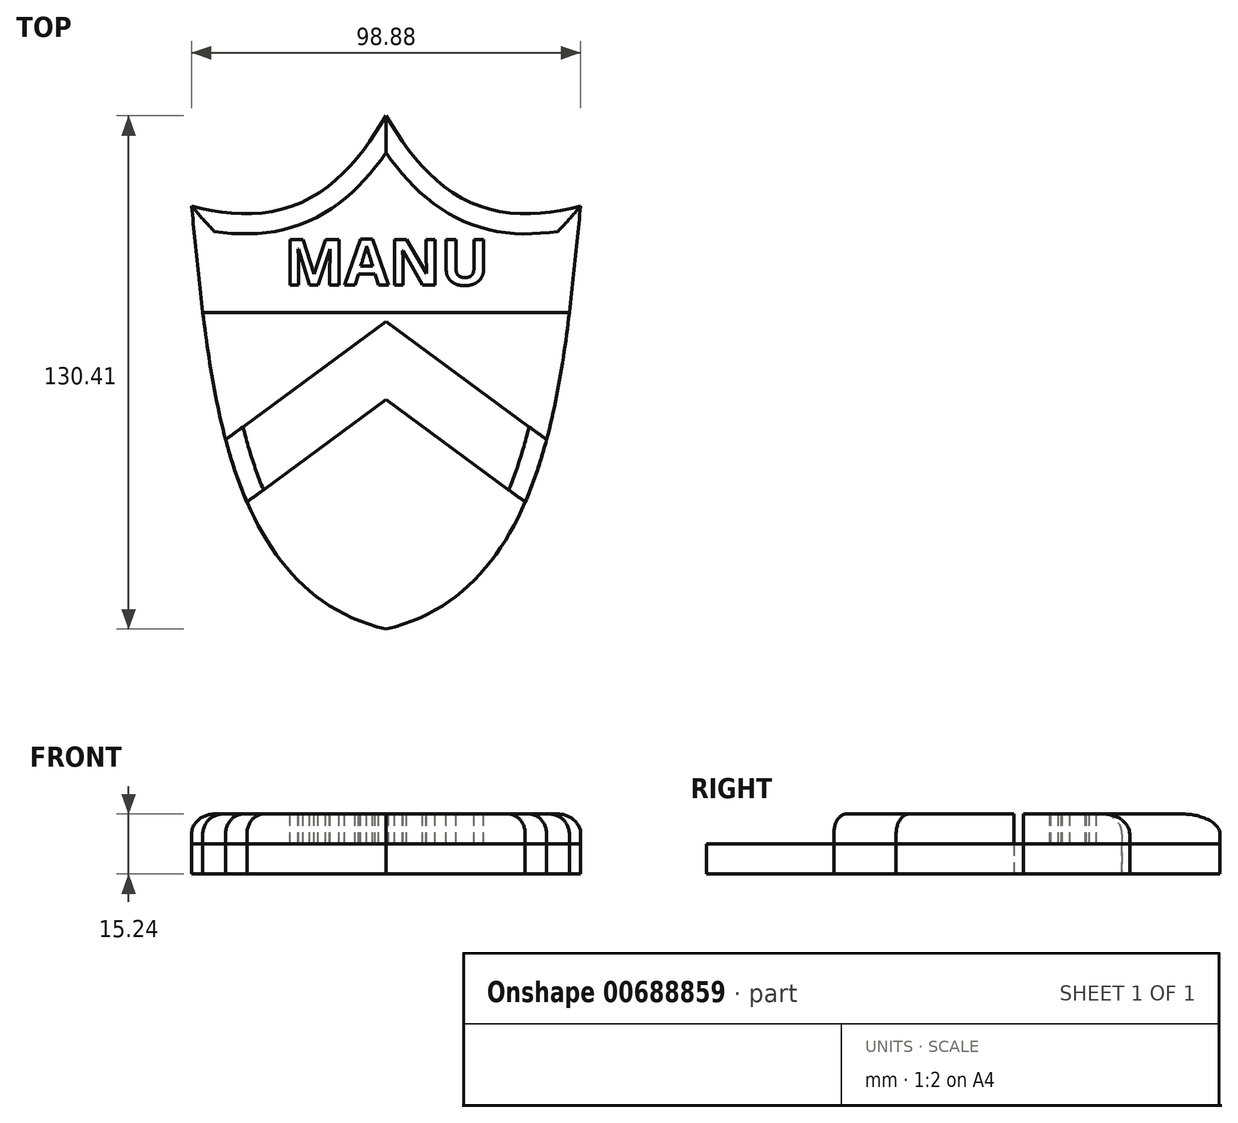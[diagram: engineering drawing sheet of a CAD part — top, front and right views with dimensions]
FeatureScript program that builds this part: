
annotation { "Feature Type Name" : "Feature", "Feature Type Description" : "" }
export const myFeature = defineFeature(function(context is Context, id is Id, definition is map)
    precondition{}
    {
        {
            var Q0;
            Q0=qCreatedBy(makeId("Top.planeOp"),FACE);
            var sketch = newSketch(context, id + "F0", { "sketchPlane" : qUnion([Q0])});
            skFitSpline(sketch, "E0", {"points": [v(-49.44, 33.32) * mm, v(0, -74.16) * mm], "startDerivative": vector(12.9, -119.66) * mm, "endDerivative": vector(128.25, -30.1) * mm});
            skFitSpline(sketch, "E1", {"points": [v(-49.44, 33.32) * mm, v(0, 56.25) * mm], "startDerivative": vector(78.1, -20.78) * mm, "endDerivative": vector(31.53, 53.02) * mm});
            skFitSpline(sketch, "E2.MirrorCS", {"points": [v(49.44, 33.32) * mm, v(0, 56.25) * mm], "startDerivative": vector(-78.1, -20.78) * mm, "endDerivative": vector(-31.53, 53.02) * mm});
            skFitSpline(sketch, "E3.MirrorCS", {"points": [v(49.44, 33.32) * mm, v(0, -74.16) * mm], "startDerivative": vector(-12.9, -119.66) * mm, "endDerivative": vector(-128.25, -30.1) * mm});
            skLineSegment(sketch, "E4", {"start": v(-46.57, 6.3) * mm, "end": v(0, 6.3) * mm});
            skLineSegment(sketch, "E5.MirrorCS", {"start": v(46.57, 6.3) * mm, "end": v(0, 6.3) * mm});
            skLineSegment(sketch, "E6", {"start": v(-40.76, -26.02) * mm, "end": v(0, 3.94) * mm});
            skLineSegment(sketch, "E7", {"start": v(-35.35, -41.87) * mm, "end": v(0, -15.88) * mm});
            skLineSegment(sketch, "E8.MirrorCS", {"start": v(40.76, -26.02) * mm, "end": v(0, 3.94) * mm});
            skLineSegment(sketch, "E9.MirrorCS", {"start": v(35.35, -41.87) * mm, "end": v(0, -15.88) * mm});
            skSolve(sketch);
        }
        {
            var Q0;
            {var subQ3=sQuery(id+"F0.wireOp",EDGE,"E1");Q0=makeQuery(id+"F0.imprint","IMPRINT",FACE,{"disambiguationData":[TD([[makeQuery(id+"F0.imprint","IMPRINT",EDGE,{"derivedFrom":subQ3}),-1.0]])]});}
            var Q1;
            {var subQ1=sQuery(id+"F0.wireOp",EDGE,"E6");Q1=makeQuery(id+"F0.imprint","IMPRINT",FACE,{"disambiguationData":[TD([[makeQuery(id+"F0.imprint","IMPRINT",EDGE,{"derivedFrom":subQ1}),-1.0]])]});}
            extrude(context, id + "F1", {"entities" : qUnion([Q0, Q1]), "depth" : 15.24 * mm, "offsetDistance" : 25.4 * mm});
        }
        {
            var Q0;
            Q0 = qSketchRegion(id + "F0", true);
            extrude(context, id + "F2", {"entities" : qUnion([Q0]), "depth" : 7.62 * mm, "offsetDistance" : 25.4 * mm});
        }
        {
            var Q0;
            Q0=makeQuery(id+"F1.opExtrude","CAP_FACE",FACE,{"disambiguationData":[OSD([sQuery(id+"F0.wireOp",EDGE,"E0"),sQuery(id+"F0.wireOp",EDGE,"E1"),sQuery(id+"F0.wireOp",EDGE,"E2.MirrorCS"),sQuery(id+"F0.wireOp",EDGE,"E3.MirrorCS"),sQuery(id+"F0.wireOp",EDGE,"E4"),sQuery(id+"F0.wireOp",EDGE,"E5.MirrorCS")])],"isStart":false});
            var sketch = newSketch(context, id + "F3", { "sketchPlane" : qUnion([Q0])});
            skText(sketch, "E10", { "text": "MANU", "fontName": "OpenSans-Bold.ttf"});
            const initialGuessF3  = {"E10": [-0.02586, 0.01326, 1, 0, 0.0117]};
            skSetInitialGuess(sketch, initialGuessF3);
            skSolve(sketch);
        }
        {
            var Q0;
            Q0 = qSketchRegion(id + "F3", true);
            extrude(context, id + "F4", {"entities" : qUnion([Q0]), "operationType" : NewBodyOperationType.REMOVE, "oppositeDirection" : true, "depth" : 7.62 * mm, "offsetDistance" : 25.4 * mm});
        }
        {
            var Q0;
            {var subQ0=sQuery(id+"F0.wireOp",EDGE,"E0");Q0=makeQuery(id+"F1.opExtrude","CAP_EDGE",EDGE,{"disambiguationData":[OSD([subQ0]),TDD([makeQuery(id+"F0.imprint","IMPRINT",EDGE,{"disambiguationData":[TD([[makeQuery(id+"F0.imprint","INTERSECT",VERTEX,{"derivedFrom":[subQ0,sQuery(id+"F0.wireOp",EDGE,"E6")]}),-1.0]])],"derivedFrom":subQ0})])],"isStart":false});}
            var Q1;
            {var subQ0=sQuery(id+"F0.wireOp",EDGE,"E3.MirrorCS");Q1=makeQuery(id+"F1.opExtrude","CAP_EDGE",EDGE,{"disambiguationData":[OSD([subQ0]),TDD([makeQuery(id+"F0.imprint","IMPRINT",EDGE,{"disambiguationData":[TD([[makeQuery(id+"F0.imprint","INTERSECT",VERTEX,{"derivedFrom":[subQ0,sQuery(id+"F0.wireOp",EDGE,"E8.MirrorCS")]}),-1.0]])],"derivedFrom":subQ0})])],"isStart":false});}
            var Q2;
            {var subQ0=sQuery(id+"F0.wireOp",EDGE,"E3.MirrorCS");Q2=makeQuery(id+"F1.opExtrude","CAP_EDGE",EDGE,{"disambiguationData":[OSD([subQ0]),TDD([makeQuery(id+"F0.imprint","IMPRINT",EDGE,{"disambiguationData":[TD([[makeQuery(id+"F0.imprint","INTERSECT",VERTEX,{"derivedFrom":[sQuery(id+"F0.wireOp",EDGE,"E2.MirrorCS"),subQ0]}),-1.0]])],"derivedFrom":subQ0})])],"isStart":false});}
            var Q3;
            {var subQ0=sQuery(id+"F0.wireOp",EDGE,"E0");Q3=makeQuery(id+"F1.opExtrude","CAP_EDGE",EDGE,{"disambiguationData":[OSD([subQ0]),TDD([makeQuery(id+"F0.imprint","IMPRINT",EDGE,{"disambiguationData":[TD([[makeQuery(id+"F0.imprint","INTERSECT",VERTEX,{"derivedFrom":[subQ0,sQuery(id+"F0.wireOp",EDGE,"E1")]}),-1.0]])],"derivedFrom":subQ0})])],"isStart":false});}
            var Q4;
            Q4=makeQuery(id+"F1.opExtrude","CAP_EDGE",EDGE,{"disambiguationData":[OSD([sQuery(id+"F0.wireOp",EDGE,"E1")])],"isStart":false});
            var Q5;
            Q5=makeQuery(id+"F1.opExtrude","CAP_EDGE",EDGE,{"disambiguationData":[OSD([sQuery(id+"F0.wireOp",EDGE,"E2.MirrorCS")])],"isStart":false});
            fillet(context, id + "F5", {"entities" : qUnion([Q0, Q1, Q2, Q3, Q4, Q5]), "radius" : 5.08 * mm, "tangentPropagation" : true, "allowEdgeOverflow" : false});
        }
    });
